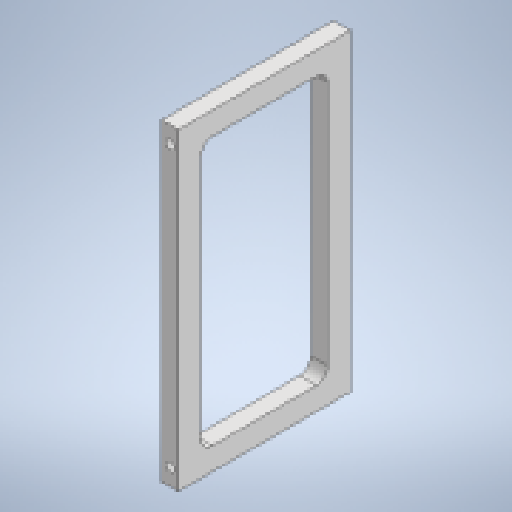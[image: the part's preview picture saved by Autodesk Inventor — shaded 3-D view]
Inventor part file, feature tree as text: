
AUTODESK INVENTOR PART (.ipt)
format: ipt  version: 2025.1 (Build 291241000, 241)  size: 195,072 bytes
history: native  units: mm
features: other x6, reference x5, sketch x4, extrude x3, hole x1, fillet x1, projected_geometry x1
ambient origin geometry x8: Origin, YZ Plane, XZ Plane, XY Plane, X Axis, Y Axis, Z Axis, Center Point
bodies: Body1 (feature_tree)
feature tree (21):
  other  "ソリッド1"
  sketch  "スケッチ1"
  other  "作業平面1"
  extrude  "押し出し1"  Depth=3.0mm
  hole  "穴1"  [1 undecoded]
  extrude  "押し出し2"  Depth=3.0mm
  fillet  "フィレット1"  Radius=10.0mm
  extrude  "押し出し3"  Depth=4.0mm
  reference  "参照1"
  reference  "参照2"
  sketch  "スケッチ2"
  reference  "参照3"
  reference  "参照4"
  sketch  "スケッチ3"
  projected_geometry  "投影ループ1"
  sketch  "スケッチ4"
  reference  "参照5"
  other  "<userpath>\Documents\Inventor\Vixen\kosi_v2.iam"
  other  "kosi_v2.iam"
  other  "piti_mata:1"
  other  "senakamata:1"
note: 1 required parameter value undecoded (feature->parameter linkage not recoverable at this tier; creation-order binding heuristic only, values carry confidence <= 0.55)
